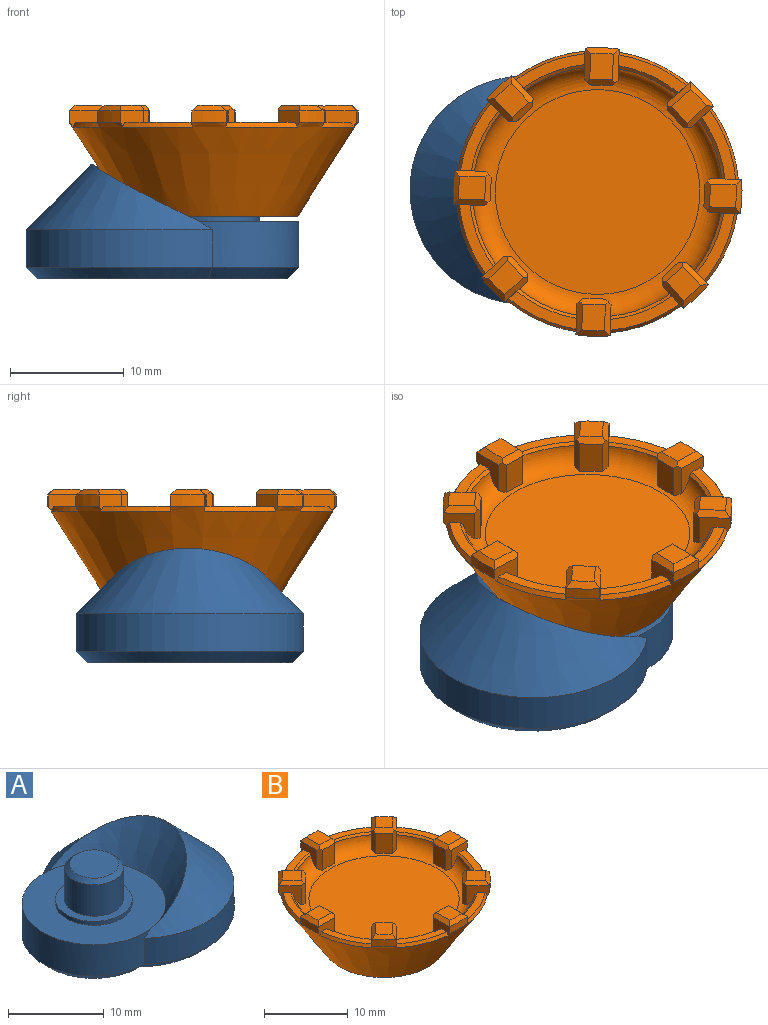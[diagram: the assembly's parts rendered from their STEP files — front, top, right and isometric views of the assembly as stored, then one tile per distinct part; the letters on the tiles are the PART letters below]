
ASSEMBLY  parts=2 mates=1
PART A: 19 faces, bbox 24x21.3x10 mm
  f0: plane 2.36x0.17mm, normal (0,0,1), area 0.2mm2, adj f5,f11
  f1: cylinder r=7.5mm len=15mm, axis (0,0,-1), area 94.1mm2, adj f2,f4,f11,f18
  f2: cylinder r=10mm len=20mm, axis (0,0,-1), area 151.4mm2, adj f1,f11,f17
  f3: plane 22x18mm, normal (0,0,-1), area 263.6mm2, adj f15,f16,f17,f18
  f4: plane 15x15mm, normal (0,0,1), area 126.4mm2, adj f1,f5,f6
  f5: cone r=7.5mm half-angle=32.6deg, axis (0,0,1), area 86.3mm2, adj f0,f4,f11
  f6: cylinder r=4mm len=8mm, axis (0,0,-1), area 12.6mm2, adj f4,f7
  f7: plane 8x8mm, normal (0,0,1), area 21mm2, adj f6,f8
  f8: cylinder r=3.05mm len=6.1mm, axis (0,0,-1), area 76.7mm2, adj f7,f10
  f9: plane 5.1x5.1mm, normal (0,0,1), area 20.4mm2, adj f10
  f10: cone r=2.55mm half-angle=45deg, axis (0,0,-1), area 12.4mm2, adj f8,f9
  f11: cone r=4.3mm half-angle=45deg, axis (0,0,-1), area 201.1mm2, adj f0,f1,f2,f5
  f12: cylinder r=3.1mm len=6.2mm, axis (0,0,-1), area 47.8mm2, adj f13,f14,f15
  f13: plane 5x3.5mm, normal (1,0,0), area 17.5mm2, adj f12,f14,f16
  f14: plane 6.2x4.93mm, normal (0,0,-1), area 25.8mm2, adj f12,f13
  f15: cone r=3.1mm half-angle=45deg, axis (0,0,-1), area 10.6mm2, adj f3,f12,f16
  f16: plane 5.5x0.51mm, normal (0.71,0,-0.71), area 3.7mm2, adj f3,f13,f15
  f17: cone r=10mm half-angle=45deg, axis (0,0,1), area 62.2mm2, adj f2,f3,f18
  f18: cone r=7.5mm half-angle=45deg, axis (0,0,1), area 31.3mm2, adj f1,f3,f17
PART B: 127 faces, bbox 25.4x25.4x9.8 mm
  f0: plane 6x3.16mm, normal (0,0,1), area 5.8mm2, adj f53,f57,f99,f100
  f1: plane 6x3.16mm, normal (0,0,1), area 5.8mm2, adj f47,f51,f101,f102
  f2: plane 6x3.16mm, normal (0,0,1), area 5.8mm2, adj f41,f45,f103,f104
  f3: plane 6x3.16mm, normal (0,0,1), area 5.8mm2, adj f35,f39,f105,f107
  f4: plane 6x3.16mm, normal (0,0,1), area 5.8mm2, adj f29,f33,f106,f108
  f5: plane 6x3.16mm, normal (0,0,1), area 5.8mm2, adj f23,f27,f109,f110
  f6: plane 6x3.16mm, normal (0,0,1), area 5.8mm2, adj f17,f21,f95,f96
  f7: cylinder r=6.42mm len=12.84mm, axis (0,0,-1), area 180.6mm2, adj f11,f94
  f8: plane 14.84x14.84mm, normal (0,0,-1), area 32.2mm2, adj f9,f94
  f9: cone r=12.7mm half-angle=32.6deg, axis (0,0,1), area 591.7mm2, adj f8,f15,f17,f18,f21,f23,f24,f27
  f10: plane 6x3.16mm, normal (0,0,1), area 5.8mm2, adj f15,f59,f97,f98
  f11: plane 12.84x12.84mm, normal (0,0,-1), area 129.5mm2, adj f7
  f12: torus R=9mm, axis (0,0,1), area 131mm2, adj f13,f14,f15,f17,f20,f21,f23,f26
  f13: plane 18x18mm, normal (0,0,1), area 254.5mm2, adj f12
  f14: plane 2.17x0.15mm, normal (0,0,-1), area 0.3mm2, adj f12,f16,f125,f126
  f15: plane 2.73x2.72mm, normal (1,0,0), area 4.1mm2, adj f9,f10,f12,f18,f83,f97,f98,f126
  f16: plane 2.93x2mm, normal (0,1,0), area 5.9mm2, adj f14,f82,f125,f126
  f17: plane 2.73x2.72mm, normal (-1,0,0), area 4.1mm2, adj f6,f9,f12,f18,f84,f95,f96,f125
  f18: cylinder r=12.7mm len=3mm, axis (0,0,-1), area 3mm2, adj f9,f15,f17,f85
  f19: plane 2.31x2mm, normal (0,0,1), area 4.6mm2, adj f82,f83,f84,f85
  f20: plane 1.53x1.53mm, normal (0,0,-1), area 0.3mm2, adj f12,f22,f123,f124
  f21: plane 2.73x1.93mm, normal (0.71,-0.71,0), area 4.1mm2, adj f6,f9,f12,f24,f91,f95,f96,f124
  f22: plane 2.93x1.41mm, normal (0.71,0.71,0), area 5.9mm2, adj f20,f90,f123,f124
  f23: plane 2.73x1.93mm, normal (-0.71,0.71,0), area 4.1mm2, adj f5,f9,f12,f24,f92,f109,f110,f123
  f24: cylinder r=12.7mm len=2.12mm, axis (0,0,-1), area 3mm2, adj f9,f21,f23,f93
  f25: plane 3.02x3.02mm, normal (0,0,1), area 4.6mm2, adj f90,f91,f92,f93
  f26: plane 2.17x0.15mm, normal (0,0,-1), area 0.3mm2, adj f12,f28,f121,f122
  f27: plane 2.73x2.72mm, normal (0,-1,0), area 4.1mm2, adj f5,f9,f12,f30,f87,f109,f110,f122
  f28: plane 2.93x2mm, normal (1,0,0), area 5.9mm2, adj f26,f86,f121,f122
  f29: plane 2.73x2.72mm, normal (0,1,0), area 4.1mm2, adj f4,f9,f12,f30,f88,f106,f108,f121
  f30: cylinder r=12.7mm len=3mm, axis (0,0,-1), area 3mm2, adj f9,f27,f29,f89
  f31: plane 2.31x2mm, normal (0,0,1), area 4.6mm2, adj f86,f87,f88,f89
  f32: plane 1.53x1.53mm, normal (0,0,-1), area 0.3mm2, adj f12,f34,f119,f120
  f33: plane 2.73x1.93mm, normal (-0.71,-0.71,0), area 4.1mm2, adj f4,f9,f12,f36,f75,f106,f108,f120
  f34: plane 2.93x1.41mm, normal (0.71,-0.71,0), area 5.9mm2, adj f32,f74,f119,f120
  f35: plane 2.73x1.93mm, normal (0.71,0.71,0), area 4.1mm2, adj f3,f9,f12,f36,f76,f105,f107,f119
  f36: cylinder r=12.7mm len=2.12mm, axis (0,0,-1), area 3mm2, adj f9,f33,f35,f77
  f37: plane 3.02x3.02mm, normal (0,0,1), area 4.6mm2, adj f74,f75,f76,f77
  f38: plane 2.17x0.15mm, normal (0,0,-1), area 0.3mm2, adj f12,f40,f117,f118
  f39: plane 2.73x2.72mm, normal (-1,0,0), area 4.1mm2, adj f3,f9,f12,f42,f63,f105,f107,f118
  f40: plane 2.93x2mm, normal (0,-1,0), area 5.9mm2, adj f38,f62,f117,f118
  f41: plane 2.73x2.72mm, normal (1,0,0), area 4.1mm2, adj f2,f9,f12,f42,f64,f103,f104,f117
  f42: cylinder r=12.7mm len=3mm, axis (0,0,-1), area 3mm2, adj f9,f39,f41,f65
  f43: plane 2.31x2mm, normal (0,0,1), area 4.6mm2, adj f62,f63,f64,f65
  f44: plane 1.53x1.53mm, normal (0,0,-1), area 0.3mm2, adj f12,f46,f115,f116
  f45: plane 2.73x1.93mm, normal (-0.71,0.71,0), area 4.1mm2, adj f2,f9,f12,f48,f67,f103,f104,f116
  f46: plane 2.93x1.41mm, normal (-0.71,-0.71,0), area 5.9mm2, adj f44,f66,f115,f116
  f47: plane 2.73x1.93mm, normal (0.71,-0.71,0), area 4.1mm2, adj f1,f9,f12,f48,f68,f101,f102,f115
  f48: cylinder r=12.7mm len=2.12mm, axis (0,0,-1), area 3mm2, adj f9,f45,f47,f69
  f49: plane 3.02x3.02mm, normal (0,0,1), area 4.6mm2, adj f66,f67,f68,f69
  f50: plane 2.17x0.15mm, normal (0,0,-1), area 0.3mm2, adj f12,f52,f113,f114
  f51: plane 2.73x2.72mm, normal (0,1,0), area 4.1mm2, adj f1,f9,f12,f54,f71,f101,f102,f114
  f52: plane 2.93x2mm, normal (-1,0,0), area 5.9mm2, adj f50,f70,f113,f114
  f53: plane 2.73x2.72mm, normal (0,-1,0), area 4.1mm2, adj f0,f9,f12,f54,f72,f99,f100,f113
  f54: cylinder r=12.7mm len=3mm, axis (0,0,-1), area 3mm2, adj f9,f51,f53,f73
  f55: plane 2.31x2mm, normal (0,0,1), area 4.6mm2, adj f70,f71,f72,f73
  f56: plane 1.53x1.53mm, normal (0,0,-1), area 0.3mm2, adj f12,f58,f111,f112
  f57: plane 2.73x1.93mm, normal (0.71,0.71,0), area 4.1mm2, adj f0,f9,f12,f60,f79,f99,f100,f112
  f58: plane 2.93x1.41mm, normal (-0.71,0.71,0), area 5.9mm2, adj f56,f78,f111,f112
  f59: plane 2.73x1.93mm, normal (-0.71,-0.71,0), area 4.1mm2, adj f9,f10,f12,f60,f80,f97,f98,f111
  f60: cylinder r=12.7mm len=2.12mm, axis (0,0,-1), area 3mm2, adj f9,f57,f59,f81
  f61: plane 3.02x3.02mm, normal (0,0,1), area 4.6mm2, adj f78,f79,f80,f81
  f62: plane 2.5x0.5mm, normal (0,-0.71,0.71), area 1.6mm2, adj f40,f43,f63,f64,f117,f118
  f63: plane 2.98x0.51mm, normal (-0.71,0,0.71), area 1.9mm2, adj f39,f43,f62,f65,f118
  f64: plane 2.98x0.51mm, normal (0.71,0,0.71), area 1.9mm2, adj f41,f43,f62,f65,f117
  f65: cone r=12.7mm half-angle=45deg, axis (0,0,-1), area 1.8mm2, adj f42,f43,f63,f64
  f66: plane 1.77x1.77mm, normal (-0.5,-0.5,0.71), area 1.6mm2, adj f46,f49,f67,f68,f115,f116
  f67: plane 2.29x1.97mm, normal (-0.5,0.5,0.71), area 1.9mm2, adj f45,f49,f66,f69,f116
  f68: plane 2.29x1.97mm, normal (0.5,-0.5,0.71), area 1.9mm2, adj f47,f49,f66,f69,f115
  f69: cone r=12.7mm half-angle=45deg, axis (0,0,-1), area 1.8mm2, adj f48,f49,f67,f68
  f70: plane 2.5x0.5mm, normal (-0.71,0,0.71), area 1.6mm2, adj f52,f55,f71,f72,f113,f114
  f71: plane 2.98x0.51mm, normal (0,0.71,0.71), area 1.9mm2, adj f51,f55,f70,f73,f114
  f72: plane 2.98x0.51mm, normal (0,-0.71,0.71), area 1.9mm2, adj f53,f55,f70,f73,f113
  f73: cone r=12.7mm half-angle=45deg, axis (0,0,-1), area 1.8mm2, adj f54,f55,f71,f72
  f74: plane 1.77x1.77mm, normal (0.5,-0.5,0.71), area 1.6mm2, adj f34,f37,f75,f76,f119,f120
  f75: plane 2.29x1.97mm, normal (-0.5,-0.5,0.71), area 1.9mm2, adj f33,f37,f74,f77,f120
  f76: plane 2.29x1.97mm, normal (0.5,0.5,0.71), area 1.9mm2, adj f35,f37,f74,f77,f119
  f77: cone r=12.7mm half-angle=45deg, axis (0,0,-1), area 1.8mm2, adj f36,f37,f75,f76
  f78: plane 1.77x1.77mm, normal (-0.5,0.5,0.71), area 1.6mm2, adj f58,f61,f79,f80,f111,f112
  f79: plane 2.29x1.97mm, normal (0.5,0.5,0.71), area 1.9mm2, adj f57,f61,f78,f81,f112
  f80: plane 2.29x1.97mm, normal (-0.5,-0.5,0.71), area 1.9mm2, adj f59,f61,f78,f81,f111
  f81: cone r=12.7mm half-angle=45deg, axis (0,0,-1), area 1.8mm2, adj f60,f61,f79,f80
  f82: plane 2.5x0.5mm, normal (0,0.71,0.71), area 1.6mm2, adj f16,f19,f83,f84,f125,f126
  f83: plane 2.98x0.51mm, normal (0.71,0,0.71), area 1.9mm2, adj f15,f19,f82,f85,f126
  f84: plane 2.98x0.51mm, normal (-0.71,0,0.71), area 1.9mm2, adj f17,f19,f82,f85,f125
  f85: cone r=12.7mm half-angle=45deg, axis (0,0,-1), area 1.8mm2, adj f18,f19,f83,f84
  f86: plane 2.5x0.5mm, normal (0.71,0,0.71), area 1.6mm2, adj f28,f31,f87,f88,f121,f122
  f87: plane 2.98x0.51mm, normal (0,-0.71,0.71), area 1.9mm2, adj f27,f31,f86,f89,f122
  f88: plane 2.98x0.51mm, normal (0,0.71,0.71), area 1.9mm2, adj f29,f31,f86,f89,f121
  f89: cone r=12.7mm half-angle=45deg, axis (0,0,-1), area 1.8mm2, adj f30,f31,f87,f88
  f90: plane 1.77x1.77mm, normal (0.5,0.5,0.71), area 1.6mm2, adj f22,f25,f91,f92,f123,f124
  f91: plane 2.29x1.97mm, normal (0.5,-0.5,0.71), area 1.9mm2, adj f21,f25,f90,f93,f124
  f92: plane 2.29x1.97mm, normal (-0.5,0.5,0.71), area 1.9mm2, adj f23,f25,f90,f93,f123
  f93: cone r=12.7mm half-angle=45deg, axis (0,0,-1), area 1.8mm2, adj f24,f25,f91,f92
  f94: cone r=6.42mm half-angle=45deg, axis (0,0,-1), area 15.9mm2, adj f7,f8
  f95: cone r=12.43mm half-angle=28.7deg, axis (0,0,-1), area 3.2mm2, adj f6,f9,f17,f21
  f96: cone r=10.99mm half-angle=48.5deg, axis (0,0,1), area 2.1mm2, adj f6,f12,f17,f21
  f97: cone r=12.43mm half-angle=28.7deg, axis (0,0,-1), area 3.2mm2, adj f9,f10,f15,f59
  f98: cone r=10.99mm half-angle=48.5deg, axis (0,0,1), area 2.1mm2, adj f10,f12,f15,f59
  f99: cone r=12.43mm half-angle=28.7deg, axis (0,0,-1), area 3.2mm2, adj f0,f9,f53,f57
  f100: cone r=10.99mm half-angle=48.5deg, axis (0,0,1), area 2.1mm2, adj f0,f12,f53,f57
  f101: cone r=10.99mm half-angle=48.5deg, axis (0,0,1), area 2.1mm2, adj f1,f12,f47,f51
  f102: cone r=12.43mm half-angle=28.7deg, axis (0,0,-1), area 3.2mm2, adj f1,f9,f47,f51
  f103: cone r=10.99mm half-angle=48.5deg, axis (0,0,1), area 2.1mm2, adj f2,f12,f41,f45
  f104: cone r=12.43mm half-angle=28.7deg, axis (0,0,-1), area 3.2mm2, adj f2,f9,f41,f45
  f105: cone r=12.43mm half-angle=28.7deg, axis (0,0,-1), area 3.2mm2, adj f3,f9,f35,f39
  f106: cone r=10.99mm half-angle=48.5deg, axis (0,0,1), area 2.1mm2, adj f4,f12,f29,f33
  f107: cone r=10.99mm half-angle=48.5deg, axis (0,0,1), area 2.1mm2, adj f3,f12,f35,f39
  f108: cone r=12.43mm half-angle=28.7deg, axis (0,0,-1), area 3.2mm2, adj f4,f9,f29,f33
  f109: cone r=10.99mm half-angle=48.5deg, axis (0,0,1), area 2.1mm2, adj f5,f12,f23,f27
  f110: cone r=12.43mm half-angle=28.7deg, axis (0,0,-1), area 3.2mm2, adj f5,f9,f23,f27
  f111: plane 3.19x0.72mm, normal (-1,0,0), area 2.1mm2, adj f12,f56,f58,f59,f78,f80
  f112: plane 3.19x0.72mm, normal (0,1,0), area 2.1mm2, adj f12,f56,f57,f58,f78,f79
  f113: plane 3.19x0.52mm, normal (-0.71,-0.71,0), area 2.1mm2, adj f12,f50,f52,f53,f70,f72
  f114: plane 3.19x0.52mm, normal (-0.71,0.71,0), area 2.1mm2, adj f12,f50,f51,f52,f70,f71
  f115: plane 3.19x0.72mm, normal (0,-1,0), area 2.1mm2, adj f12,f44,f46,f47,f66,f68
  f116: plane 3.19x0.72mm, normal (-1,0,0), area 2.1mm2, adj f12,f44,f45,f46,f66,f67
  f117: plane 3.19x0.52mm, normal (0.71,-0.71,0), area 2.1mm2, adj f12,f38,f40,f41,f62,f64
  f118: plane 3.19x0.52mm, normal (-0.71,-0.71,0), area 2.1mm2, adj f12,f38,f39,f40,f62,f63
  f119: plane 3.19x0.72mm, normal (1,0,0), area 2.1mm2, adj f12,f32,f34,f35,f74,f76
  f120: plane 3.19x0.72mm, normal (0,-1,0), area 2.1mm2, adj f12,f32,f33,f34,f74,f75
  f121: plane 3.19x0.52mm, normal (0.71,0.71,0), area 2.1mm2, adj f12,f26,f28,f29,f86,f88
  f122: plane 3.19x0.52mm, normal (0.71,-0.71,0), area 2.1mm2, adj f12,f26,f27,f28,f86,f87
  f123: plane 3.19x0.72mm, normal (0,1,0), area 2.1mm2, adj f12,f20,f22,f23,f90,f92
  f124: plane 3.19x0.72mm, normal (1,0,0), area 2.1mm2, adj f12,f20,f21,f22,f90,f91
  f125: plane 3.19x0.52mm, normal (-0.71,0.71,0), area 2.1mm2, adj f12,f14,f16,f17,f82,f84
  f126: plane 3.19x0.52mm, normal (0.71,0.71,0), area 2.1mm2, adj f12,f14,f15,f16,f82,f83
PLACE A rot(axis=(0,0,1),178.3deg) t=(0,0,0)mm
PLACE B rot(axis=(0,0,1),178.2deg) t=(6.5,-0.19,5.5)mm
MATE revolute A.f1 <-> B.f7  axis (0,0,1) through (6.5,-0.19,5.5)mm
